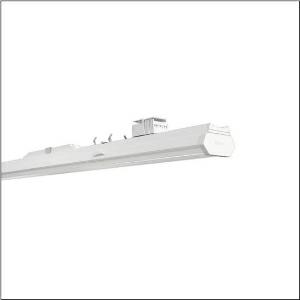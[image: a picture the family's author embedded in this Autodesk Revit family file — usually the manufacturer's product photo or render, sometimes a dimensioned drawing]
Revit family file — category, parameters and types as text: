
# Revit family: licross_r__11_protected_ho_51tp11dn4f5s_1ce9
name_source: partatom
category: Lighting Fixtures
units: mm (PartAtom-declared; Revit-internal decimal feet)

## family parameters
Cut with Voids When Loaded = No
Host = Face
Light Source = No
Part Type = Normal
Room Calculation Point = No
Round Connector Dimension = Use Diameter
Shared = No

## types (1)
- --- (1 x LED, 15510 lm, 87.3 W, 4000K)
    Apparent Load = 87 VA
    CIE Flux Codes = 84 94 98 99 100
    Color Rendering = 80
    Color Temperature = 4000K
    Default Elevation = 1800 mm
    Description = Licross® 11 Protected HO, luminaire insert, of sheet steel, galvanised, coil coated, white, length: 1.500mm, width: 90mm, height: 101mm, LED rated luminous flux: 15.510lm, light colour: 840, control gear: DALI 2, with plug, 5-pole, with phase selection, mains connection: 220..240V, AC, 50/60Hz, rated input power: 87W, internal wiring halogen-free, primary light control with lens, of plastic, primary optical cover: cover, of PMMA, light emission: direct distribution, primary light characteristic: symmetric, protection rating (complete): IP64, insulation class (complete): insulation class I (protective earthing), certification: CE, ENEC, VDE, UKCA, protection symbol: D if used in an environment with conductive dust loads with corresponding accessories, impact resistance: IK06, permissible ambient temperature for indoor applications: -25..+30°C, corresponds to IFS (International Featured Standards) requirements for safety and quality in the food industry, reducing of maximum allowable ambient temperature of 5°C with ceiling mounting, LABS conformity tested according to VDMA 24364:2018-05, packaging unit: 1 piece
    Height = 92 mm
    Lamp = 1 x LED
    Lamp Light Flux = 15510 lm
    Lamp Power = 87.3 W
    Lamp count = 1
    Length = 1500 mm
    Luminous efficacy = 178 lm/W
    Manufacturer = Siteco
    ModVariant = No
    Model = 51TP11DN4F5S
    Mounting Place = Ceiling
    Mounting Type = Pendant
    Number of Poles = 1
    OnlyDefault = Yes
    Power Factor = 1
    Product Name = Licross® 11 Protected HO
    Product group = luminaire insert | ceiling pendant
    ProductGroupID = 902
    Protection Class = Protection class I
    Protection Degree = IP 64
    RLX_Detail_Level = 1
    RLX_Emergency_Light_Flux = 0 lm
    RLX_Emergency_Type = 0
    RLX_Emergency_Type_DB = No
    RlxData = <blob elided: 24321 chars, md5=7286e7f1>
    Socket = socket
    Standby Power = 0 W
    System Light Flux = 15510 lm
    System Power = 87 W
    Type Comments = factory setting: luminous flux: 100 % | dim-lin: 254 | 589 mA
    Type Image = l_1256148.jpg
    URL = http://relux.com
    VarID = @adj_122449
    Voltage = 0 V
    Weight = 0.00 kg
    Width = 88 mm

## geometry (parser evidence)
native form markers: Blend x4, Sweep x10
no freeform markers — native parametric forms only
